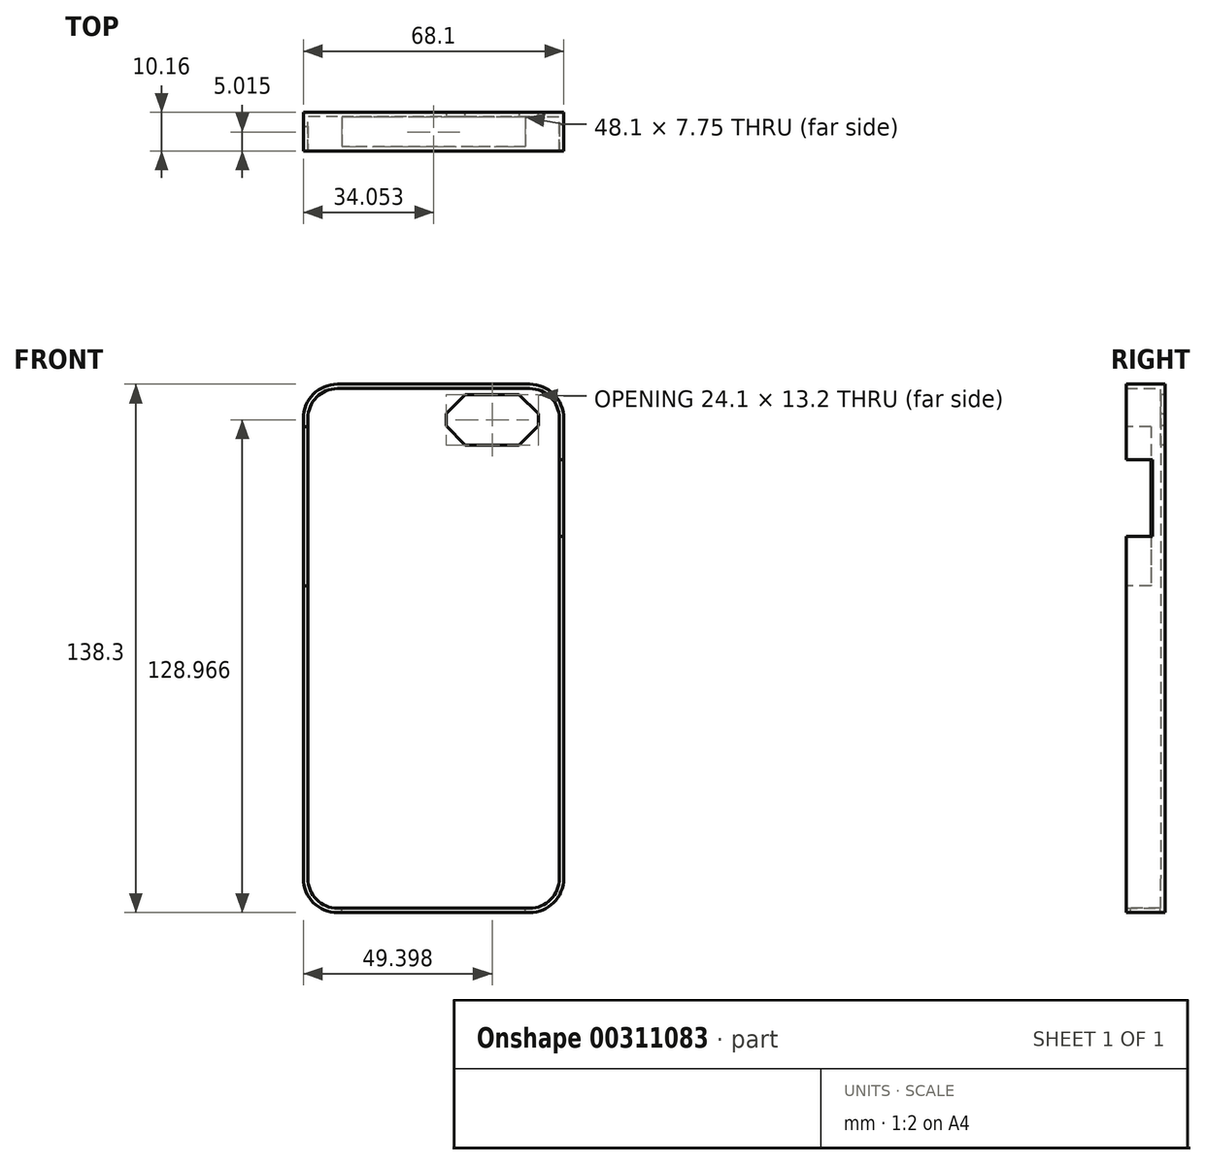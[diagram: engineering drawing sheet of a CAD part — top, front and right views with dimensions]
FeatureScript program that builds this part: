
annotation { "Feature Type Name" : "Feature", "Feature Type Description" : "" }
export const myFeature = defineFeature(function(context is Context, id is Id, definition is map)
    precondition{}
    {
        {
            var Q0;
            Q0=qCreatedBy(makeId("Front.planeOp"),FACE);
            var sketch = newSketch(context, id + "F0", { "sketchPlane" : qUnion([Q0])});
            skLineSegment(sketch, "E0.bottom", {"start": v(34.05, 69.15) * mm, "end": v(-34.05, 69.15) * mm});
            skLineSegment(sketch, "E0.top", {"start": v(34.05, -69.15) * mm, "end": v(-34.05, -69.15) * mm});
            skLineSegment(sketch, "E0.left", {"start": v(34.05, 69.15) * mm, "end": v(34.05, -69.15) * mm});
            skLineSegment(sketch, "E0.right", {"start": v(-34.05, 69.15) * mm, "end": v(-34.05, -69.15) * mm});
            skPoint(sketch, "E0.middle", {"position": v(0, 0) * mm});
            skSolve(sketch);
        }
        {
            var Q0;
            Q0=makeQuery(id+"F0.imprint","IMPRINT",FACE,{"disambiguationData":[TD([[makeQuery(id+"F0.imprint","IMPRINT",EDGE,{"derivedFrom":sQuery(id+"F0.wireOp",EDGE,"E0.bottom")}),1.0]])]});
            extrude(context, id + "F1", {"entities" : qUnion([Q0]), "endBound" : BoundingType.SYMMETRIC, "depth" : 10.16 * mm});
        }
        {
            var Q0;
            Q0=makeQuery(id+"F1.opExtrude","SWEPT_EDGE",EDGE,{"disambiguationData":[OSD([sQuery(id+"F0.wireOp",EDGE,"E0.bottom"),sQuery(id+"F0.wireOp",EDGE,"E0.right")])]});
            var Q1;
            Q1=makeQuery(id+"F1.opExtrude","SWEPT_EDGE",EDGE,{"disambiguationData":[OSD([sQuery(id+"F0.wireOp",EDGE,"E0.bottom"),sQuery(id+"F0.wireOp",EDGE,"E0.left")])]});
            var Q2;
            Q2=makeQuery(id+"F1.opExtrude","SWEPT_EDGE",EDGE,{"disambiguationData":[OSD([sQuery(id+"F0.wireOp",EDGE,"E0.top"),sQuery(id+"F0.wireOp",EDGE,"E0.left")])]});
            var Q3;
            Q3=makeQuery(id+"F1.opExtrude","SWEPT_EDGE",EDGE,{"disambiguationData":[OSD([sQuery(id+"F0.wireOp",EDGE,"E0.top"),sQuery(id+"F0.wireOp",EDGE,"E0.right")])]});
            fillet(context, id + "F2", {"entities" : qUnion([Q0, Q1, Q2, Q3]), "radius" : 8.93 * mm, "tangentPropagation" : true, "allowEdgeOverflow" : false});
        }
        {
            var Q0;
            Q0=makeQuery(id+"F1.opExtrude","CAP_FACE",FACE,{"disambiguationData":[OSD([sQuery(id+"F0.wireOp",EDGE,"E0.bottom"),sQuery(id+"F0.wireOp",EDGE,"E0.top"),sQuery(id+"F0.wireOp",EDGE,"E0.left"),sQuery(id+"F0.wireOp",EDGE,"E0.right")])],"isStart":false});
            shell(context, id + "F3", {"entities" : qUnion([Q0]), "thickness" : 1.15 * mm});
        }
        {
            var Q0;
            Q0=makeQuery(id+"F0.imprint","IMPRINT",FACE,{"disambiguationData":[TD([[makeQuery(id+"F0.imprint","IMPRINT",EDGE,{"derivedFrom":sQuery(id+"F0.wireOp",EDGE,"E0.bottom")}),1.0]])]});
            var sketch = newSketch(context, id + "F4", { "sketchPlane" : qUnion([Q0])});
            skLineSegment(sketch, "E1.bottom", {"start": v(27.4, 66.41) * mm, "end": v(3.3, 66.41) * mm});
            skLineSegment(sketch, "E1.top", {"start": v(27.4, 53.22) * mm, "end": v(3.3, 53.22) * mm});
            skLineSegment(sketch, "E1.left", {"start": v(27.4, 66.41) * mm, "end": v(27.4, 53.22) * mm});
            skLineSegment(sketch, "E1.right", {"start": v(3.3, 66.41) * mm, "end": v(3.3, 53.22) * mm});
            skSolve(sketch);
        }
        {
            var Q0;
            Q0=qSketchRegion(id+"F4",true);
            extrude(context, id + "F5", {"entities" : qUnion([Q0]), "operationType" : NewBodyOperationType.REMOVE, "endBound" : BoundingType.SYMMETRIC, "depth" : 25 * mm});
        }
        {
            var Q0;
            Q0=makeQuery(id+"F1.opExtrude","SWEPT_FACE",FACE,{"disambiguationData":[OSD([sQuery(id+"F0.wireOp",EDGE,"E0.top")])]});
            var sketch = newSketch(context, id + "F6", { "sketchPlane" : qUnion([Q0])});
            skLineSegment(sketch, "E2.bottom", {"start": v(-24.05, 3.94) * mm, "end": v(24.05, 3.94) * mm});
            skLineSegment(sketch, "E2.top", {"start": v(-24.05, -3.81) * mm, "end": v(24.05, -3.81) * mm});
            skLineSegment(sketch, "E2.left", {"start": v(-24.05, 3.94) * mm, "end": v(-24.05, -3.81) * mm});
            skLineSegment(sketch, "E2.right", {"start": v(24.05, 3.94) * mm, "end": v(24.05, -3.81) * mm});
            skSolve(sketch);
        }
        {
            var Q0;
            {var subQ0=sQuery(id+"F6.wireOp",EDGE,"E2.bottom");Q0=makeQuery(id+"F6.imprint","IMPRINT",FACE,{"disambiguationData":[TD([[makeQuery(id+"F6.imprint","IMPRINT",EDGE,{"derivedFrom":subQ0}),-1.0]])]});}
            var Q1;
            {var subQ0=sQuery(id+"F6.wireOp",EDGE,"E2.top");Q1=makeQuery(id+"F6.imprint","IMPRINT",FACE,{"disambiguationData":[TD([[makeQuery(id+"F6.imprint","IMPRINT",EDGE,{"derivedFrom":subQ0}),1.0]])]});}
            extrude(context, id + "F7", {"entities" : qUnion([Q0, Q1]), "operationType" : NewBodyOperationType.REMOVE, "endBound" : BoundingType.SYMMETRIC, "depth" : 25 * mm});
        }
        {
            var Q0;
            Q0=makeQuery(id+"F1.opExtrude","SWEPT_FACE",FACE,{"disambiguationData":[OSD([sQuery(id+"F0.wireOp",EDGE,"E0.right")])]});
            var sketch = newSketch(context, id + "F8", { "sketchPlane" : qUnion([Q0])});
            skLineSegment(sketch, "E3.bottom", {"start": v(-1.38, 58.06) * mm, "end": v(8.73, 58.06) * mm});
            skLineSegment(sketch, "E3.top", {"start": v(-1.38, 16.4) * mm, "end": v(8.73, 16.4) * mm});
            skLineSegment(sketch, "E3.left", {"start": v(-1.38, 58.06) * mm, "end": v(-1.38, 16.4) * mm});
            skLineSegment(sketch, "E3.right", {"start": v(8.73, 58.06) * mm, "end": v(8.73, 16.4) * mm});
            skSolve(sketch);
        }
        {
            var Q0;
            Q0=qSketchRegion(id+"F8",true);
            extrude(context, id + "F9", {"entities" : qUnion([Q0]), "operationType" : NewBodyOperationType.REMOVE, "endBound" : BoundingType.SYMMETRIC, "depth" : 25 * mm});
        }
        {
            var Q0;
            Q0=makeQuery(id+"F1.opExtrude","SWEPT_FACE",FACE,{"disambiguationData":[OSD([sQuery(id+"F0.wireOp",EDGE,"E0.left")])]});
            var sketch = newSketch(context, id + "F10", { "sketchPlane" : qUnion([Q0])});
            skLineSegment(sketch, "E4.bottom", {"start": v(-5.08, 49.35) * mm, "end": v(1.78, 49.35) * mm});
            skLineSegment(sketch, "E4.top", {"start": v(-5.08, 29.37) * mm, "end": v(1.78, 29.37) * mm});
            skLineSegment(sketch, "E4.left", {"start": v(-5.08, 49.35) * mm, "end": v(-5.08, 29.37) * mm});
            skLineSegment(sketch, "E4.right", {"start": v(1.78, 49.35) * mm, "end": v(1.78, 29.37) * mm});
            skSolve(sketch);
        }
        {
            var Q0;
            Q0=makeQuery(id+"F10.imprint","IMPRINT",FACE,{"disambiguationData":[TD([[makeQuery(id+"F10.imprint","IMPRINT",EDGE,{"derivedFrom":sQuery(id+"F10.wireOp",EDGE,"E4.bottom")}),-1.0]])]});
            extrude(context, id + "F11", {"entities" : qUnion([Q0]), "operationType" : NewBodyOperationType.REMOVE, "endBound" : BoundingType.SYMMETRIC, "depth" : 25 * mm});
        }
        {
            var Q0;
            Q0=makeQuery(id+"F5.boolean.opBoolean","COPY",EDGE,{"derivedFrom":makeQuery(id+"F5.opExtrude","SWEPT_EDGE",EDGE,{"disambiguationData":[OSD([sQuery(id+"F4.wireOp",EDGE,"E1.bottom"),sQuery(id+"F4.wireOp",EDGE,"E1.right")])]})});
            var Q1;
            Q1=makeQuery(id+"F5.boolean.opBoolean","COPY",EDGE,{"derivedFrom":makeQuery(id+"F5.opExtrude","SWEPT_EDGE",EDGE,{"disambiguationData":[OSD([sQuery(id+"F4.wireOp",EDGE,"E1.bottom"),sQuery(id+"F4.wireOp",EDGE,"E1.left")])]})});
            var Q2;
            Q2=makeQuery(id+"F5.boolean.opBoolean","COPY",EDGE,{"derivedFrom":makeQuery(id+"F5.opExtrude","SWEPT_EDGE",EDGE,{"disambiguationData":[OSD([sQuery(id+"F4.wireOp",EDGE,"E1.top"),sQuery(id+"F4.wireOp",EDGE,"E1.left")])]})});
            var Q3;
            Q3=makeQuery(id+"F5.boolean.opBoolean","COPY",EDGE,{"derivedFrom":makeQuery(id+"F5.opExtrude","SWEPT_EDGE",EDGE,{"disambiguationData":[OSD([sQuery(id+"F4.wireOp",EDGE,"E1.top"),sQuery(id+"F4.wireOp",EDGE,"E1.right")])]})});
            chamfer(context, id + "F12", {"entities" : qUnion([Q0, Q1, Q2, Q3]), "width" : 5 * mm, "tangentPropagation" : true});
        }
    });
